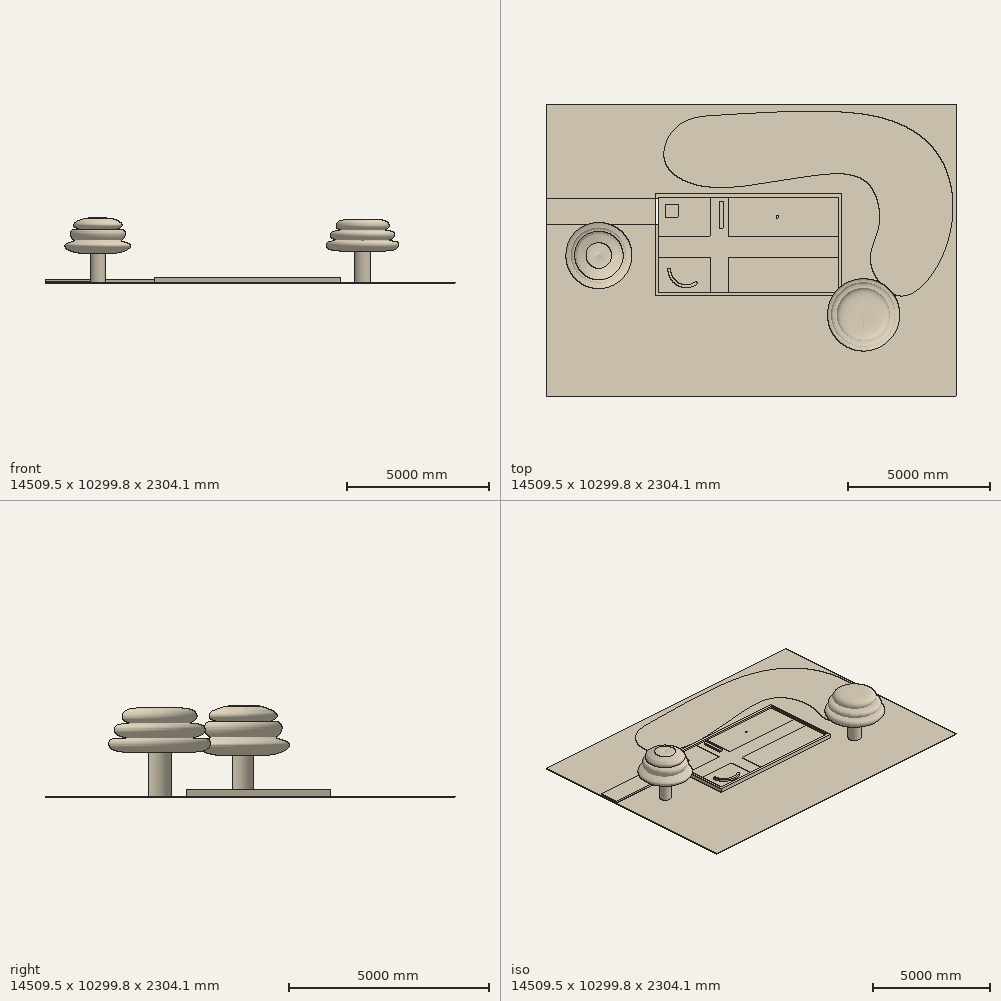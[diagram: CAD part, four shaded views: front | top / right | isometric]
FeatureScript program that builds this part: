
annotation { "Feature Type Name" : "Feature", "Feature Type Description" : "" }
export const myFeature = defineFeature(function(context is Context, id is Id, definition is map)
    precondition{}
    {
        {
            var Q0;
            Q0=qCreatedBy(makeId("Top.planeOp"),FACE);
            var sketch = newSketch(context, id + "F0", { "sketchPlane" : qUnion([Q0])});
            skLineSegment(sketch, "E0.bottom", {"start": v(0, 0) * mm, "end": v(6365.24, 0) * mm});
            skLineSegment(sketch, "E0.top", {"start": v(0, 3352.8) * mm, "end": v(6365.24, 3352.8) * mm});
            skLineSegment(sketch, "E0.left", {"start": v(0, 0) * mm, "end": v(0, 3352.8) * mm});
            skLineSegment(sketch, "E0.right", {"start": v(6365.24, 0) * mm, "end": v(6365.24, 3352.8) * mm});
            skCircle(sketch, "E1", {"center": v(4199.6, 2677.96) * mm, "radius": 53.97 * mm});
            skLineSegment(sketch, "E2.bottom", {"start": v(253.1, 3095.14) * mm, "end": v(710.3, 3095.14) * mm});
            skLineSegment(sketch, "E2.top", {"start": v(253.1, 2637.94) * mm, "end": v(710.3, 2637.94) * mm});
            skLineSegment(sketch, "E2.left", {"start": v(253.1, 3095.14) * mm, "end": v(253.1, 2637.94) * mm});
            skLineSegment(sketch, "E2.right", {"start": v(710.3, 3095.14) * mm, "end": v(710.3, 2637.94) * mm});
            skCircle(sketch, "E3", {"center": v(4199.6, 2677.96) * mm, "radius": 5.29 * mm});
            skPoint(sketch, "E4.centerSnap0", {"position": v(253.1, 2866.54) * mm});
            skPoint(sketch, "E4.centerSnap1", {"position": v(481.7, 3095.14) * mm});
            skLineSegment(sketch, "E5.bottom", {"start": v(-126, -123.37) * mm, "end": v(6478, -123.37) * mm});
            skLineSegment(sketch, "E5.top", {"start": v(-126, 3483.43) * mm, "end": v(6478, 3483.43) * mm});
            skLineSegment(sketch, "E5.left", {"start": v(-126, -123.37) * mm, "end": v(-126, 3483.43) * mm});
            skLineSegment(sketch, "E5.right", {"start": v(6478, -123.37) * mm, "end": v(6478, 3483.43) * mm});
            skLineSegment(sketch, "E6", {"start": v(-126, 3483.43) * mm, "end": v(0, 3352.8) * mm});
            skLineSegment(sketch, "E7", {"start": v(-126, -123.37) * mm, "end": v(0, 0) * mm});
            skLineSegment(sketch, "E8", {"start": v(6478, -123.37) * mm, "end": v(6365.24, 0) * mm});
            skLineSegment(sketch, "E9", {"start": v(6478, 3483.43) * mm, "end": v(6365.24, 3352.8) * mm});
            skLineSegment(sketch, "E10", {"start": v(-126, 1290.53) * mm, "end": v(0, 1290.53) * mm});
            skLineSegment(sketch, "E11", {"start": v(1375.82, -123.37) * mm, "end": v(1375.82, 0) * mm});
            skLineSegment(sketch, "E12", {"start": v(3756.75, -123.37) * mm, "end": v(3756.75, 0) * mm});
            skLineSegment(sketch, "E13", {"start": v(6365.24, 1092.73) * mm, "end": v(6478, 1092.73) * mm});
            skLineSegment(sketch, "E14", {"start": v(6365.24, 2484.66) * mm, "end": v(6478, 2484.66) * mm});
            skLineSegment(sketch, "E15", {"start": v(3798.74, 3483.43) * mm, "end": v(3798.74, 3352.8) * mm});
            skLineSegment(sketch, "E16", {"start": v(1285.95, 3483.43) * mm, "end": v(1285.95, 3352.8) * mm});
            skArc(sketch, "E17", {"start": v(421.44, 834.95) * mm, "mid": v(728.57, 320.85) * mm, "end": v(1324.19, 383.03) * mm});
            skArc(sketch, "E18.0", {"start": v(319.89, 837.96) * mm, "mid": v(683.09, 230) * mm, "end": v(1387.45, 303.54) * mm});
            skLineSegment(sketch, "E19", {"start": v(319.89, 837.96) * mm, "end": v(421.44, 834.95) * mm});
            skLineSegment(sketch, "E20", {"start": v(1387.45, 303.54) * mm, "end": v(1324.19, 383.03) * mm});
            skLineSegment(sketch, "E21.bottom", {"start": v(2152.72, 3221.53) * mm, "end": v(2305.12, 3221.53) * mm});
            skLineSegment(sketch, "E21.top", {"start": v(2152.72, 2256.33) * mm, "end": v(2305.12, 2256.33) * mm});
            skLineSegment(sketch, "E21.left", {"start": v(2152.72, 3221.53) * mm, "end": v(2152.72, 2256.33) * mm});
            skLineSegment(sketch, "E21.right", {"start": v(2305.12, 3221.53) * mm, "end": v(2305.12, 2256.33) * mm});
            skLineSegment(sketch, "E22.bottom", {"start": v(0, 2388.21) * mm, "end": v(-2133.6, 2388.21) * mm});
            skLineSegment(sketch, "E22.top", {"start": v(0, 3302.61) * mm, "end": v(-2133.6, 3302.61) * mm});
            skLineSegment(sketch, "E22.left", {"start": v(0, 2388.21) * mm, "end": v(0, 3302.61) * mm});
            skLineSegment(sketch, "E22.right", {"start": v(-2133.6, 2388.21) * mm, "end": v(-2133.6, 3302.61) * mm});
            skLineSegment(sketch, "E23", {"start": v(1832.05, 3352.8) * mm, "end": v(1832.05, 1965.16) * mm});
            skLineSegment(sketch, "E24", {"start": v(1832.05, 1965.16) * mm, "end": v(0, 1965.16) * mm});
            skLineSegment(sketch, "E25", {"start": v(2483.4, 3352.8) * mm, "end": v(2483.4, 1965.16) * mm});
            skLineSegment(sketch, "E26", {"start": v(2483.4, 1965.16) * mm, "end": v(6365.24, 1965.16) * mm});
            skLineSegment(sketch, "E27", {"start": v(1832.05, 0) * mm, "end": v(1832.05, 1235.63) * mm});
            skLineSegment(sketch, "E28", {"start": v(1832.05, 1235.63) * mm, "end": v(0, 1235.63) * mm});
            skLineSegment(sketch, "E29", {"start": v(2483.4, 0) * mm, "end": v(2483.4, 1235.63) * mm});
            skLineSegment(sketch, "E30", {"start": v(2483.4, 1235.63) * mm, "end": v(6365.24, 1235.63) * mm});
            skLineSegment(sketch, "E31.bottom", {"start": v(-3974.23, 6628.56) * mm, "end": v(10535.28, 6628.56) * mm});
            skLineSegment(sketch, "E31.top", {"start": v(-3974.23, -3671.25) * mm, "end": v(10535.28, -3671.25) * mm});
            skLineSegment(sketch, "E31.left", {"start": v(-3974.23, 6628.56) * mm, "end": v(-3974.23, -3671.25) * mm});
            skLineSegment(sketch, "E31.right", {"start": v(10535.28, 6628.56) * mm, "end": v(10535.28, -3671.25) * mm});
            skCircle(sketch, "E32", {"center": v(-2118.17, 1295.8) * mm, "radius": 258.96 * mm});
            skLineSegment(sketch, "E33", {"start": v(-2133.6, 2388.21) * mm, "end": v(-3974.23, 2388.21) * mm});
            skLineSegment(sketch, "E34", {"start": v(-2133.6, 3302.61) * mm, "end": v(-3974.23, 3302.61) * mm});
            skCircle(sketch, "E35", {"center": v(7251.18, -794.02) * mm, "radius": 288.27 * mm});
            skFitSpline(sketch, "E36", {"points": [v(2810.32, 6311.36) * mm, v(720.5, 5910.8) * mm, v(198.05, 4691.75) * mm, v(1573.84, 3751.33) * mm, v(5387.76, 4117.05) * mm, v(7373.08, 3873.24) * mm, v(7791.05, 2340.7) * mm, v(7494.99, 1051.99) * mm, v(8557.31, -132.24) * mm, v(10142.09, 1522.2) * mm, v(10072.43, 4552.43) * mm, v(7756.22, 6206.87) * mm, v(2810.32, 6311.36) * mm]});
            skSolve(sketch);
        }
        {
            var Q0;
            {var subQ0=sQuery(id+"F0.wireOp",EDGE,"61w1Zbx0-8IyF-onGd-JFbY-M6TZgRs2bGoE");Q0=makeQuery(id+"F0.imprint","IMPRINT",FACE,{"disambiguationData":[TD([[makeQuery(id+"F0.imprint","IMPRINT",EDGE,{"derivedFrom":subQ0}),-1.0]])]});}
            var Q1;
            {var subQ0=sQuery(id+"F0.wireOp",EDGE,"E7");Q1=makeQuery(id+"F0.imprint","IMPRINT",FACE,{"disambiguationData":[TD([[makeQuery(id+"F0.imprint","IMPRINT",EDGE,{"derivedFrom":subQ0}),1.0]])]});}
            var Q2;
            {var subQ0=sQuery(id+"F0.wireOp",EDGE,"E7");Q2=makeQuery(id+"F0.imprint","IMPRINT",FACE,{"disambiguationData":[TD([[makeQuery(id+"F0.imprint","IMPRINT",EDGE,{"derivedFrom":subQ0}),-1.0]])]});}
            var Q3;
            {var subQ0=sQuery(id+"F0.wireOp",EDGE,"E11");Q3=makeQuery(id+"F0.imprint","IMPRINT",FACE,{"disambiguationData":[TD([[makeQuery(id+"F0.imprint","IMPRINT",EDGE,{"derivedFrom":subQ0}),-1.0]])]});}
            var Q4;
            {var subQ0=sQuery(id+"F0.wireOp",EDGE,"E8");Q4=makeQuery(id+"F0.imprint","IMPRINT",FACE,{"disambiguationData":[TD([[makeQuery(id+"F0.imprint","IMPRINT",EDGE,{"derivedFrom":subQ0}),1.0]])]});}
            var Q5;
            {var subQ0=sQuery(id+"F0.wireOp",EDGE,"E8");Q5=makeQuery(id+"F0.imprint","IMPRINT",FACE,{"disambiguationData":[TD([[makeQuery(id+"F0.imprint","IMPRINT",EDGE,{"derivedFrom":subQ0}),-1.0]])]});}
            var Q6;
            {var subQ0=sQuery(id+"F0.wireOp",EDGE,"E13");Q6=makeQuery(id+"F0.imprint","IMPRINT",FACE,{"disambiguationData":[TD([[makeQuery(id+"F0.imprint","IMPRINT",EDGE,{"derivedFrom":subQ0}),1.0]])]});}
            var Q7;
            {var subQ0=sQuery(id+"F0.wireOp",EDGE,"E9");Q7=makeQuery(id+"F0.imprint","IMPRINT",FACE,{"disambiguationData":[TD([[makeQuery(id+"F0.imprint","IMPRINT",EDGE,{"derivedFrom":subQ0}),1.0]])]});}
            var Q8;
            {var subQ0=sQuery(id+"F0.wireOp",EDGE,"E9");Q8=makeQuery(id+"F0.imprint","IMPRINT",FACE,{"disambiguationData":[TD([[makeQuery(id+"F0.imprint","IMPRINT",EDGE,{"derivedFrom":subQ0}),-1.0]])]});}
            var Q9;
            {var subQ0=sQuery(id+"F0.wireOp",EDGE,"E15");Q9=makeQuery(id+"F0.imprint","IMPRINT",FACE,{"disambiguationData":[TD([[makeQuery(id+"F0.imprint","IMPRINT",EDGE,{"derivedFrom":subQ0}),-1.0]])]});}
            var Q10;
            {var subQ0=sQuery(id+"F0.wireOp",EDGE,"E6");Q10=makeQuery(id+"F0.imprint","IMPRINT",FACE,{"disambiguationData":[TD([[makeQuery(id+"F0.imprint","IMPRINT",EDGE,{"derivedFrom":subQ0}),1.0]])]});}
            var Q11;
            {var subQ0=sQuery(id+"F0.wireOp",EDGE,"E6");Q11=makeQuery(id+"F0.imprint","IMPRINT",FACE,{"disambiguationData":[TD([[makeQuery(id+"F0.imprint","IMPRINT",EDGE,{"derivedFrom":subQ0}),-1.0]])]});}
            var Q12;
            {var subQ0=sQuery(id+"F0.wireOp",EDGE,"E10");Q12=makeQuery(id+"F0.imprint","IMPRINT",FACE,{"disambiguationData":[TD([[makeQuery(id+"F0.imprint","IMPRINT",EDGE,{"derivedFrom":subQ0}),1.0]])]});}
            extrude(context, id + "F1", {"entities" : qUnion([Q0, Q1, Q2, Q3, Q4, Q5, Q6, Q7, Q8, Q9, Q10, Q11, Q12]), "depth" : 203.2 * mm});
        }
        {
            var Q0;
            Q0=makeQuery(id+"F0.imprint","IMPRINT",FACE,{"disambiguationData":[TD([[makeQuery(id+"F0.imprint","IMPRINT",EDGE,{"derivedFrom":sQuery(id+"F0.wireOp",EDGE,"E2.bottom")}),-1.0]])]});
            extrude(context, id + "F2", {"entities" : qUnion([Q0]), "depth" : 127 * mm});
        }
        {
            var Q0;
            Q0=makeQuery(id+"F0.imprint","IMPRINT",FACE,{"disambiguationData":[TD([[makeQuery(id+"F0.imprint","IMPRINT",EDGE,{"derivedFrom":sQuery(id+"F0.wireOp",EDGE,"E17")}),-1.0]])]});
            extrude(context, id + "F3", {"entities" : qUnion([Q0]), "depth" : 203.2 * mm});
        }
        {
            var Q0;
            Q0=makeQuery(id+"F0.imprint","IMPRINT",FACE,{"disambiguationData":[TD([[makeQuery(id+"F0.imprint","IMPRINT",EDGE,{"derivedFrom":sQuery(id+"F0.wireOp",EDGE,"E21.bottom")}),-1.0]])]});
            extrude(context, id + "F4", {"entities" : qUnion([Q0]), "depth" : 203.2 * mm});
        }
        {
            var Q0;
            Q0=makeQuery(id+"F0.imprint","IMPRINT",FACE,{"disambiguationData":[TD([[makeQuery(id+"F0.imprint","IMPRINT",EDGE,{"derivedFrom":sQuery(id+"F0.wireOp",EDGE,"E1")}),1.0]])]});
            extrude(context, id + "F5", {"entities" : qUnion([Q0]), "depth" : 19 * mm});
        }
        {
            var Q0;
            {var subQ5=sQuery(id+"F0.wireOp",EDGE,"E22.left");Q0=makeQuery(id+"F0.imprint","IMPRINT",FACE,{"disambiguationData":[TD([[makeQuery(id+"F0.imprint","IMPRINT",EDGE,{"derivedFrom":subQ5}),1.0]])]});}
            var Q1;
            {var subQ5=sQuery(id+"F0.wireOp",EDGE,"E22.right");Q1=makeQuery(id+"F0.imprint","IMPRINT",FACE,{"disambiguationData":[TD([[makeQuery(id+"F0.imprint","IMPRINT",EDGE,{"derivedFrom":subQ5}),-1.0]])]});}
            var Q2;
            Q2=makeQuery(id+"F0.imprint","IMPRINT",FACE,{"disambiguationData":[TD([[makeQuery(id+"F0.imprint","IMPRINT",EDGE,{"derivedFrom":sQuery(id+"F0.wireOp",EDGE,"E22.right")}),1.0]])]});
            extrude(context, id + "F6", {"entities" : qUnion([Q0, Q1, Q2]), "depth" : 127 * mm});
        }
        {
            var Q0;
            Q0=makeQuery(id+"F0.imprint","IMPRINT",FACE,{"disambiguationData":[TD([[makeQuery(id+"F0.imprint","IMPRINT",EDGE,{"derivedFrom":sQuery(id+"F0.wireOp",EDGE,"E21.bottom")}),1.0]])]});
            var Q1;
            {var subQ1=sQuery(id+"F0.wireOp",EDGE,"E0.left");var subQ5=makeQuery(id+"F0.imprint","INTERSECT",VERTEX,{"derivedFrom":[subQ1,sQuery(id+"F0.wireOp",EDGE,"E10")]});Q1=makeQuery(id+"F0.imprint","IMPRINT",FACE,{"disambiguationData":[TD([[makeQuery(id+"F0.imprint","IMPRINT",EDGE,{"disambiguationData":[TD([[subQ5,1.0]])],"derivedFrom":subQ1}),-1.0]])]});}
            var Q2;
            {var subQ10=sQuery(id+"F0.wireOp",EDGE,"E29");Q2=makeQuery(id+"F0.imprint","IMPRINT",FACE,{"disambiguationData":[TD([[makeQuery(id+"F0.imprint","IMPRINT",EDGE,{"derivedFrom":subQ10}),1.0]])]});}
            extrude(context, id + "F7", {"entities" : qUnion([Q0, Q1, Q2]), "depth" : 127 * mm});
        }
        {
            var Q0;
            {var subQ5=sQuery(id+"F0.wireOp",EDGE,"E17");Q0=makeQuery(id+"F0.imprint","IMPRINT",FACE,{"disambiguationData":[TD([[makeQuery(id+"F0.imprint","IMPRINT",EDGE,{"derivedFrom":subQ5}),1.0]])]});}
            var Q1;
            Q1=makeQuery(id+"F0.imprint","IMPRINT",FACE,{"disambiguationData":[TD([[makeQuery(id+"F0.imprint","IMPRINT",EDGE,{"derivedFrom":sQuery(id+"F0.wireOp",EDGE,"E18.0")}),-1.0]])]});
            var Q2;
            {var subQ6=sQuery(id+"F0.wireOp",EDGE,"E29");Q2=makeQuery(id+"F0.imprint","IMPRINT",FACE,{"disambiguationData":[TD([[makeQuery(id+"F0.imprint","IMPRINT",EDGE,{"derivedFrom":subQ6}),-1.0]])]});}
            var Q3;
            Q3=makeQuery(id+"F0.imprint","IMPRINT",FACE,{"disambiguationData":[TD([[makeQuery(id+"F0.imprint","IMPRINT",EDGE,{"derivedFrom":sQuery(id+"F0.wireOp",EDGE,"E1")}),-1.0]])]});
            var Q4;
            Q4=makeQuery(id+"F0.imprint","IMPRINT",FACE,{"disambiguationData":[TD([[makeQuery(id+"F0.imprint","IMPRINT",EDGE,{"derivedFrom":sQuery(id+"F0.wireOp",EDGE,"E2.bottom")}),1.0]])]});
            extrude(context, id + "F8", {"entities" : qUnion([Q0, Q1, Q2, Q3, Q4]), "depth" : 127 * mm});
        }
        {
            var Q0;
            {var subQ19=sQuery(id+"F0.wireOp",EDGE,"E22.right");Q0=makeQuery(id+"F0.imprint","IMPRINT",FACE,{"disambiguationData":[TD([[makeQuery(id+"F0.imprint","IMPRINT",EDGE,{"derivedFrom":subQ19}),1.0]])]});}
            extrude(context, id + "F9", {"entities" : qUnion([Q0]), "depth" : 50.8 * mm});
        }
        {
            var Q0;
            Q0=makeQuery(id+"F0.imprint","IMPRINT",FACE,{"disambiguationData":[TD([[makeQuery(id+"F0.imprint","IMPRINT",EDGE,{"derivedFrom":sQuery(id+"F0.wireOp",EDGE,"E32")}),1.0]])]});
            extrude(context, id + "F10", {"entities" : qUnion([Q0]), "depth" : 1524 * mm});
        }
        {
            var Q0;
            {var subQ10=sQuery(id+"F0.wireOp",EDGE,"E31.bottom");Q0=makeQuery(id+"F0.imprint","IMPRINT",FACE,{"disambiguationData":[TD([[makeQuery(id+"F0.imprint","IMPRINT",EDGE,{"derivedFrom":subQ10}),-1.0]])]});}
            extrude(context, id + "F11", {"entities" : qUnion([Q0]), "depth" : 25.4 * mm});
        }
        {
            var Q0;
            Q0=makeQuery(id+"F10.opExtrude","CAP_EDGE",EDGE,{"disambiguationData":[OSD([sQuery(id+"F0.wireOp",EDGE,"E32")])],"isStart":false});
            cPlane(context, id + "F12", {"entities" : qUnion([Q0]), "cplaneType" : CPlaneType.LINE_ANGLE, "offset" : 25.4 * mm, "angle" : 360 * degree, "width" : 152.4 * mm, "height" : 152.4 * mm});
        }
        {
            var Q0;
            Q0=qCreatedBy(id+"F12.planeOp",FACE);
            var sketch = newSketch(context, id + "F13", { "sketchPlane" : qUnion([Q0])});
            skLineSegment(sketch, "E37", {"start": v(1297.9, 2257.6) * mm, "end": v(1297.9, 1149) * mm});
            skFitSpline(sketch, "E38", {"points": [v(1297.9, 2257.6) * mm, v(1965.27, 1904.61) * mm], "startDerivative": vector(1422.99, 546.03) * mm, "endDerivative": vector(-1638.1, -397.11) * mm});
            skFitSpline(sketch, "E39", {"points": [v(1965.27, 1904.61) * mm, v(2213.47, 1573.69) * mm, v(2125.22, 1496.47) * mm, v(2461.66, 1336.52) * mm, v(1297.9, 1149) * mm], "startDerivative": vector(4836.32, 644.84) * mm, "endDerivative": vector(-4659.04, 1798.23) * mm});
            skFitSpline(sketch, "E40", {"points": [v(1297.9, 2257.6) * mm, v(1297.9, 2538.6) * mm, v(1456.93, 2507.06) * mm, v(1639.87, 2361.97) * mm, v(1751.65, 2287.16) * mm], "startDerivative": vector(-210.71, 1237.77) * mm, "endDerivative": vector(524.22, -313.62) * mm});
            skSolve(sketch);
        }
        {
            var Q0;
            Q0=makeQuery(id+"F13.imprint","IMPRINT",FACE,{"disambiguationData":[TD([[makeQuery(id+"F13.imprint","IMPRINT",EDGE,{"derivedFrom":sQuery(id+"F13.wireOp",EDGE,"E37")}),1.0]])]});
            var Q1;
            Q1=sQuery(id+"F13.wireOp",EDGE,"E37");
            revolve(context, id + "F14", {"entities" : qUnion([Q0]), "axis" : qUnion([Q1]), "revolveType" : RevolveType.FULL});
        }
        {
            var Q0;
            Q0=makeQuery(id+"F0.imprint","IMPRINT",FACE,{"disambiguationData":[TD([[makeQuery(id+"F0.imprint","IMPRINT",EDGE,{"derivedFrom":sQuery(id+"F0.wireOp",EDGE,"E35")}),1.0]])]});
            extrude(context, id + "F15", {"entities" : qUnion([Q0]), "depth" : 1524 * mm});
        }
        {
            var Q0;
            Q0=makeQuery(id+"F15.opExtrude","CAP_EDGE",EDGE,{"disambiguationData":[OSD([sQuery(id+"F0.wireOp",EDGE,"E35")])],"isStart":false});
            cPlane(context, id + "F16", {"entities" : qUnion([Q0]), "cplaneType" : CPlaneType.LINE_ANGLE, "offset" : 25.4 * mm, "angle" : 360 * degree, "width" : 152.4 * mm, "height" : 152.4 * mm});
        }
        {
            var Q0;
            Q0=qCreatedBy(id+"F16.planeOp",FACE);
            var sketch = newSketch(context, id + "F17", { "sketchPlane" : qUnion([Q0])});
            skFitSpline(sketch, "E41", {"points": [v(-801.08, 2247.53) * mm, v(-1343.06, 2247.53) * mm, v(-1690.5, 2144.8) * mm, v(-1708.79, 1943.65) * mm, v(-1530.5, 1852.22) * mm, v(-1708.79, 1847.65) * mm, v(-1923.66, 1765.36) * mm, v(-1887.08, 1587.07) * mm, v(-1608.21, 1481.92) * mm, v(-1763.65, 1486.5) * mm, v(-2033.38, 1445.35) * mm, v(-2079.1, 1308.2) * mm, v(-1919.08, 1171.12) * mm, v(-801.08, 1171.12) * mm], "startDerivative": vector(-5197.83, 146.1) * mm, "endDerivative": vector(8828.7, 667.15) * mm});
            skLineSegment(sketch, "E42", {"start": v(-801.08, 2247.53) * mm, "end": v(-801.08, 1171.12) * mm});
            skSolve(sketch);
        }
        {
            var Q0;
            Q0=makeQuery(id+"F17.imprint","IMPRINT",FACE,{"disambiguationData":[TD([[makeQuery(id+"F17.imprint","IMPRINT",EDGE,{"derivedFrom":sQuery(id+"F17.wireOp",EDGE,"E41")}),1.0]])]});
            var Q1;
            Q1=sQuery(id+"F17.wireOp",EDGE,"E42");
            revolve(context, id + "F18", {"entities" : qUnion([Q0]), "axis" : qUnion([Q1]), "revolveType" : RevolveType.FULL});
        }
        {
            var Q0;
            Q0=makeQuery(id+"F0.imprint","IMPRINT",FACE,{"disambiguationData":[TD([[makeQuery(id+"F0.imprint","IMPRINT",EDGE,{"derivedFrom":sQuery(id+"F0.wireOp",EDGE,"E36")}),1.0]])]});
            extrude(context, id + "F19", {"entities" : qUnion([Q0]), "depth" : 25.4 * mm});
        }
    });
